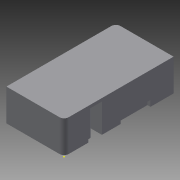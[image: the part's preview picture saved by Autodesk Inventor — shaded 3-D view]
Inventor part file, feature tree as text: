
AUTODESK INVENTOR PART (.ipt)
format: ipt  version: 2015 (Build 190159000, 159)  size: 215,552 bytes
history: native  units: in
note: dims shown in document units (in); Inventor stores cm internally (conversion verified against a paired STEP export)
features: extrude x9, sketch x8, fillet x2, projected_geometry x2
ambient origin geometry x8: Origin, YZ Plane, XZ Plane, XY Plane, X Axis, Y Axis, Z Axis, Center Point
bodies: Solid1 (feature_tree)
feature tree (21):
  extrude  "Extrusion1"  Depth=0.966in
  sketch  "Sketch2"  dims[d5=0.075in d6=0.1in d7=0.1in]
  fillet  "Fillet1"  Radius=0.533in
  fillet  "Fillet2"  Radius=0.075in
  extrude  "Extrusion2"  Depth=0.1in
  extrude  "Extrusion3"  Depth=0.125in
  extrude  "Extrusion4"  Depth=0.1in
  sketch  "Sketch6"  dims[d15=0.1in d16=0.1in]
  extrude  "Extrusion5"  Depth=0.1in
  sketch  "Sketch7"  dims[d17=0.1in d18=0.483in]
  extrude  "Extrusion7"  Depth=0.483in
  extrude  "Extrusion8"  Depth=0.1in
  extrude  "Extrusion9"  Depth=0.1in
  extrude  "Extrusion10"  Depth=0.1in
  sketch  "Sketch1"  dims[d0=1.833in d1=0.966in d2=0.533in d3=0.0in d4=0.075in]
  sketch  "Sketch4"  dims[d8=0.1in d9=0.1in d11=0.125in]
  sketch  "Sketch5"  dims[d13=0.2in d14=0.1in]
  sketch  "Sketch8"  dims[d19=0.0in d20=0.1in]
  projected_geometry  "Projected Loop1"
  sketch  "Sketch9"  dims[d21=0.24in d22=0.1in d23=0.545in d24=0.5in d25=0.45in d26=0.9in d27=0.533in d28=0.0in d29=0.279in d30=0.185in d32=0.3in d33=0.1in d34=0.533in d35=0.0in d36=0.1718in d37=1.2625in d38=0.025in d39=0.0in d40=0.05in d41=0.1in d42=0.025in d43=0.025in d46=0.05in d47=0.025in d48=0.0in d49=0.025in d50=0.0in d51=0.1in d52=0.5in d53=0.05in d54=0.0in d55=0.1in d56=0.0in]
  projected_geometry  "Projected Loop2"
